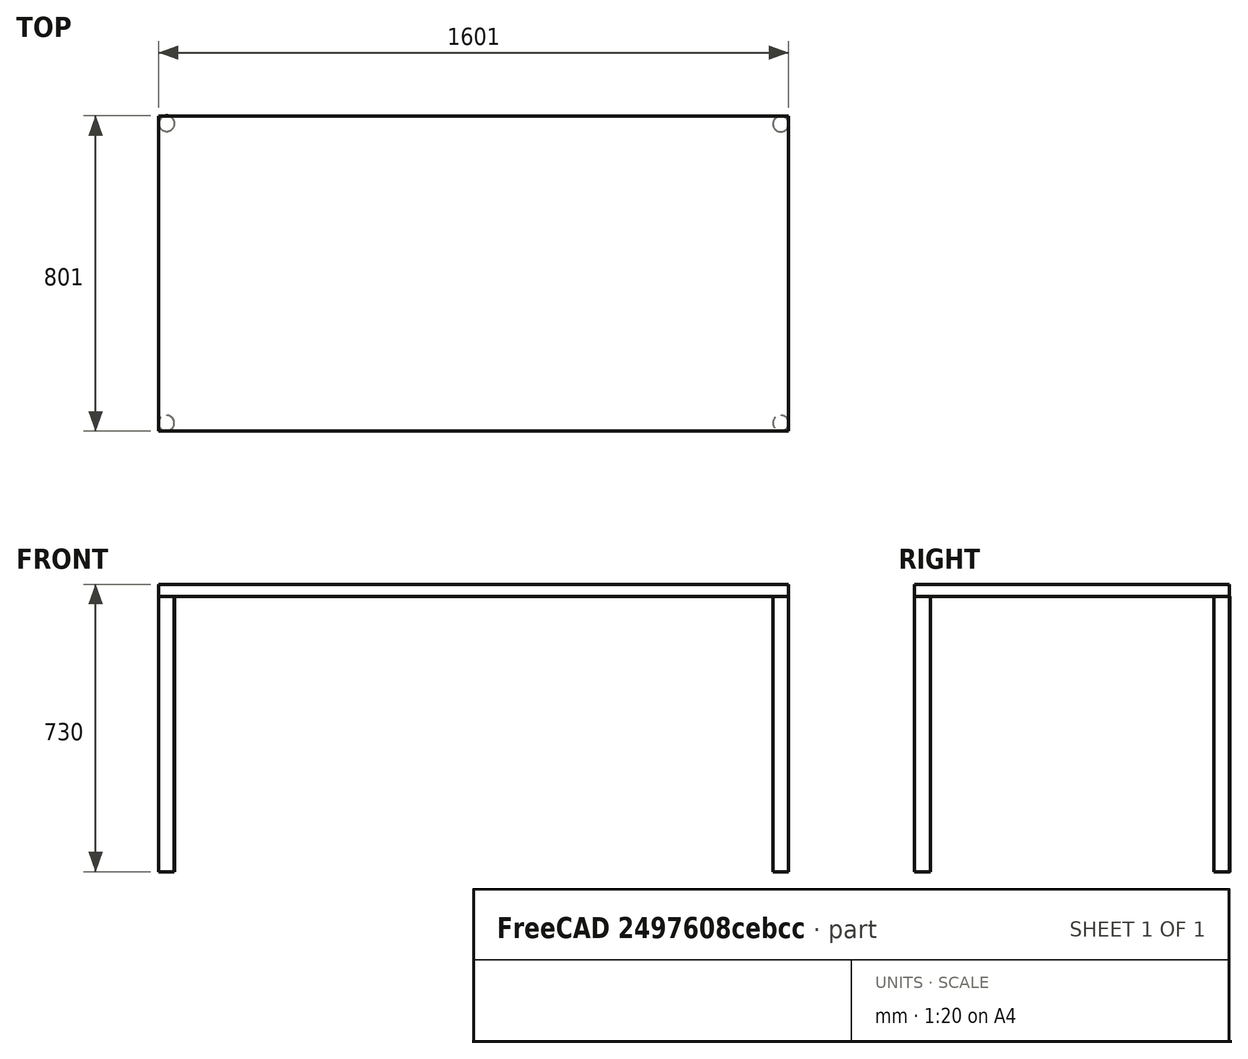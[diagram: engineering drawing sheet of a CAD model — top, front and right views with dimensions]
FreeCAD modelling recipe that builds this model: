
FCSTD DOCUMENT  (FreeCAD 0.15R4671 (Git))
Label: table_1m6_0m8_0m7
License: All rights reserved
LicenseURL: http://en.wikipedia.org/wiki/All_rights_reserved
objects: Part::Cylinder×4, Part::Box×1, Part::MultiFuse×1
note: 6 computed .brp shape members not serialized (recipe doc carries the construction recipe); baked Part::Feature solids carry a one-line shape summary decoded from their .brp

FEATURE [Part::Box] Box  label="Cube"
  Height = 30
  Length = 1600
  Placement = pos=(-800,-400,700) rot=(0,0,1;0rad)
  Width = 800
FEATURE [Part::Cylinder] Cylinder
  Angle = 360
  Height = 700
  Placement = pos=(780,380,0) rot=(0,0,1;0rad)
  Radius = 20
FEATURE [Part::Cylinder] Cylinder001
  Angle = 360
  Height = 700
  Placement = pos=(780,-380,0) rot=(0,0,1;0rad)
  Radius = 20
FEATURE [Part::Cylinder] Cylinder002
  Angle = 360
  Height = 700
  Placement = pos=(-780,381,0) rot=(0,0,1;0rad)
  Radius = 20
FEATURE [Part::Cylinder] Cylinder003
  Angle = 360
  Height = 700
  Placement = pos=(-781,-380,0) rot=(0,0,1;0rad)
  Radius = 20
FEATURE [Part::MultiFuse] Fusion
  Shapes = -> [Cylinder003,Cylinder002,Cylinder001,Cylinder,Box]
